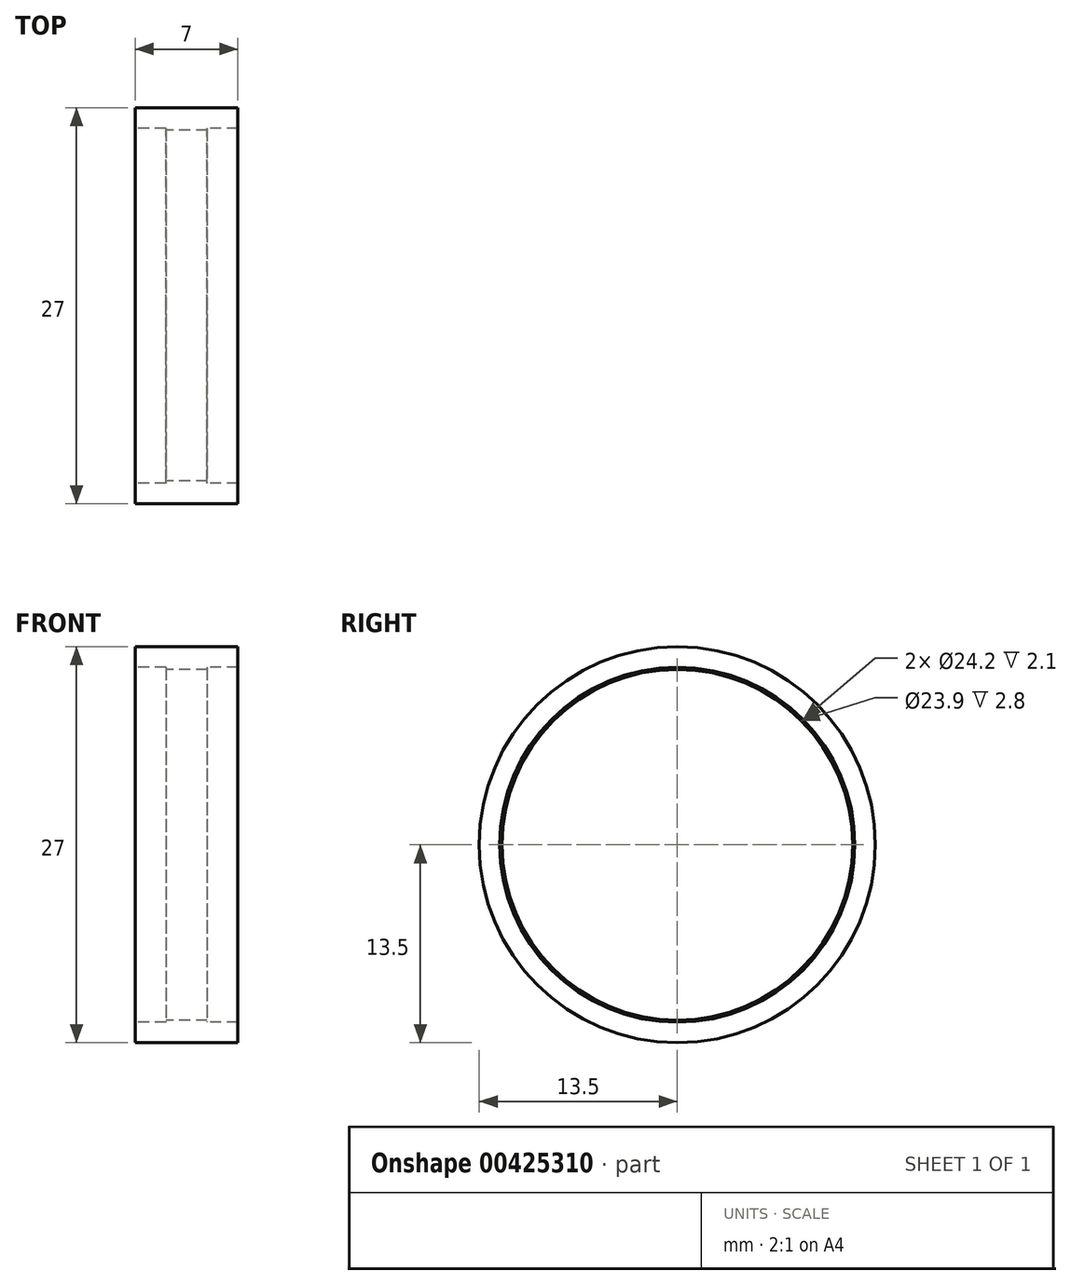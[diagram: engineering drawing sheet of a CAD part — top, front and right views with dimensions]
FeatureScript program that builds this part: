
annotation { "Feature Type Name" : "Feature", "Feature Type Description" : "" }
export const myFeature = defineFeature(function(context is Context, id is Id, definition is map)
    precondition{}
    {
        {
            var Q0;
            Q0=qCreatedBy(makeId("Front.planeOp"),FACE);
            var sketch = newSketch(context, id + "F0", { "sketchPlane" : qUnion([Q0])});
            skLineSegment(sketch, "E0.bottom", {"start": v(3.5, 13.5) * mm, "end": v(-3.5, 13.5) * mm});
            skLineSegment(sketch, "E0.top", {"start": v(3.5, 11.95) * mm, "end": v(-3.5, 11.95) * mm});
            skLineSegment(sketch, "E0.right", {"start": v(-3.5, 13.5) * mm, "end": v(-3.5, 11.95) * mm});
            skPoint(sketch, "E1", {"position": v(0, 11.95) * mm});
            skLineSegment(sketch, "E2", {"start": v(3.5, 13.5) * mm, "end": v(3.5, 11.95) * mm});
            skLineSegment(sketch, "E3", {"start": v(-3.5, 0) * mm, "end": v(3.5, 0) * mm});
            skLineSegment(sketch, "E4.bottom", {"start": v(-3.5, 11.95) * mm, "end": v(-1.4, 11.95) * mm});
            skLineSegment(sketch, "E4.top", {"start": v(-3.5, 12.1) * mm, "end": v(-1.4, 12.1) * mm});
            skLineSegment(sketch, "E4.left", {"start": v(-3.5, 11.95) * mm, "end": v(-3.5, 12.1) * mm});
            skLineSegment(sketch, "E4.right", {"start": v(-1.4, 11.95) * mm, "end": v(-1.4, 12.1) * mm});
            skLineSegment(sketch, "E5.bottom", {"start": v(3.5, 11.95) * mm, "end": v(1.4, 11.95) * mm});
            skLineSegment(sketch, "E5.top", {"start": v(3.5, 12.1) * mm, "end": v(1.4, 12.1) * mm});
            skLineSegment(sketch, "E5.left", {"start": v(3.5, 11.95) * mm, "end": v(3.5, 12.1) * mm});
            skLineSegment(sketch, "E5.right", {"start": v(1.4, 11.95) * mm, "end": v(1.4, 12.1) * mm});
            skSolve(sketch);
        }
        {
            var Q0;
            Q0=makeQuery(id+"F0.imprint","IMPRINT",FACE,{"disambiguationData":[TD([[makeQuery(id+"F0.imprint","IMPRINT",EDGE,{"derivedFrom":sQuery(id+"F0.wireOp",EDGE,"E0.bottom")}),1.0]])]});
            var Q1;
            Q1=sQuery(id+"F0.wireOp",EDGE,"E3");
            revolve(context, id + "F1", {"entities" : qUnion([Q0]), "axis" : qUnion([Q1]), "revolveType" : RevolveType.FULL});
        }
    });
